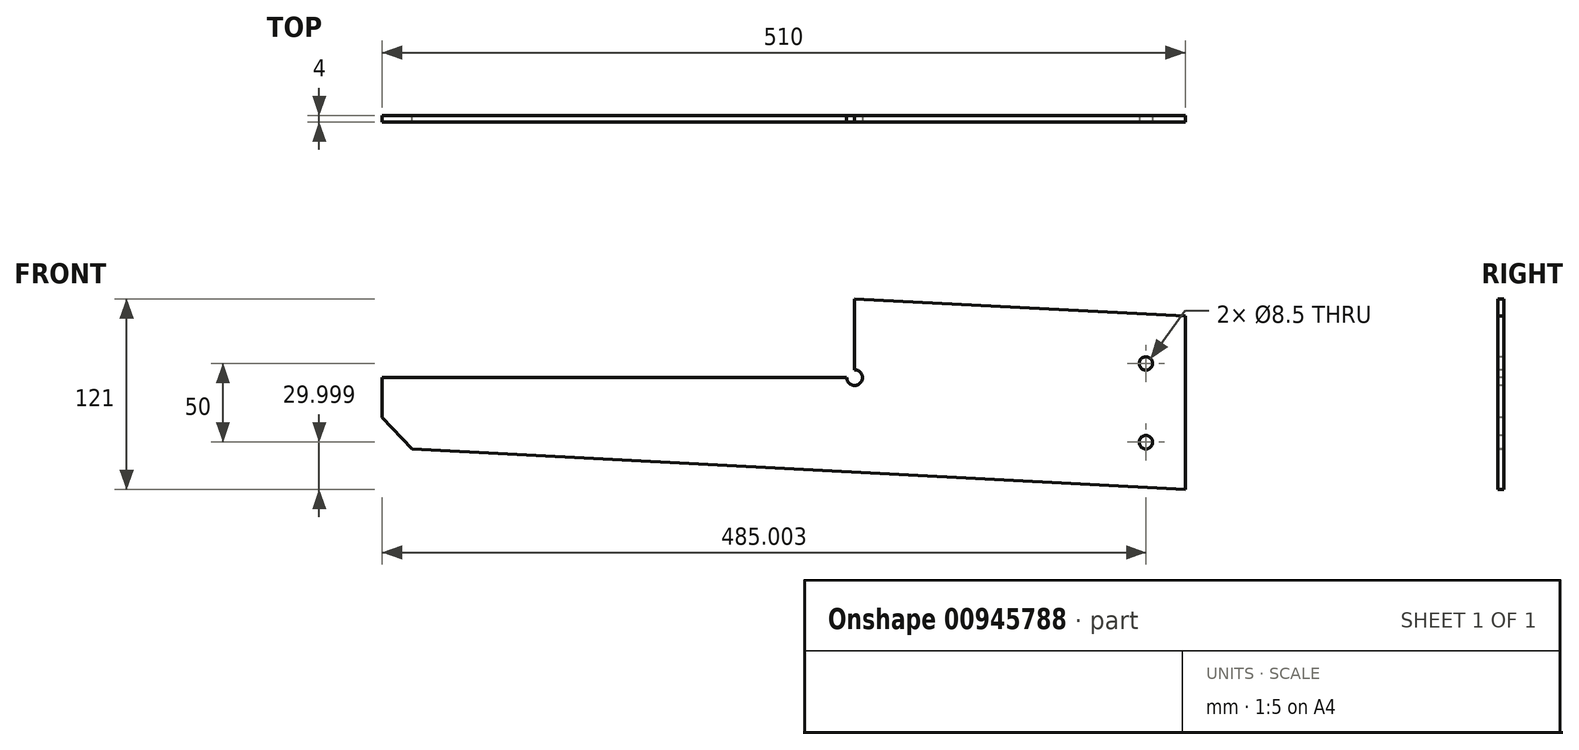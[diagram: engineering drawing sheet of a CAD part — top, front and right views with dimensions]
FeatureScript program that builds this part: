
annotation { "Feature Type Name" : "Feature", "Feature Type Description" : "" }
export const myFeature = defineFeature(function(context is Context, id is Id, definition is map)
    precondition{}
    {
        {
            var Q0;
            Q0=qCreatedBy(makeId("Front.planeOp"),FACE);
            var sketch = newSketch(context, id + "F0", { "sketchPlane" : qUnion([Q0])});
            skLineSegment(sketch, "E0", {"start": v(-207.34, -21.2) * mm, "end": v(92.66, -21.2) * mm});
            skLineSegment(sketch, "E1", {"start": v(92.66, -21.2) * mm, "end": v(92.66, 28.8) * mm});
            skLineSegment(sketch, "E2", {"start": v(92.66, 28.8) * mm, "end": v(302.66, 17.79) * mm});
            skLineSegment(sketch, "E3", {"start": v(302.66, 17.79) * mm, "end": v(302.66, -92.21) * mm});
            skLineSegment(sketch, "E4", {"start": v(302.66, -92.21) * mm, "end": v(-207.34, -65.48) * mm});
            skLineSegment(sketch, "E5", {"start": v(-207.34, -65.48) * mm, "end": v(-207.34, -21.2) * mm});
            skLineSegment(sketch, "E6", {"start": v(92.66, -21.2) * mm, "end": v(92.66, -81.2) * mm});
            skSolve(sketch);
        }
        {
            var Q0;
            Q0 = qSketchRegion(id + "F0", true);
            extrude(context, id + "F1", {"entities" : qUnion([Q0]), "depth" : 4 * mm, "offsetDistance" : 25 * mm});
        }
        {
            var Q0;
            Q0=makeQuery(id+"F1.opExtrude","SWEPT_EDGE",EDGE,{"disambiguationData":[OSD([sQuery(id+"F0.wireOp",EDGE,"E4"),sQuery(id+"F0.wireOp",EDGE,"E5")])]});
            chamfer(context, id + "F2", {"entities" : qUnion([Q0]), "width" : 20 * mm, "tangentPropagation" : true});
        }
        {
            var Q0;
            Q0=makeQuery(id+"F1.opExtrude","CAP_FACE",FACE,{"disambiguationData":[OSD([sQuery(id+"F0.wireOp",EDGE,"E0"),sQuery(id+"F0.wireOp",EDGE,"E1"),sQuery(id+"F0.wireOp",EDGE,"E2"),sQuery(id+"F0.wireOp",EDGE,"E3"),sQuery(id+"F0.wireOp",EDGE,"E4"),sQuery(id+"F0.wireOp",EDGE,"E5")])],"isStart":false});
            var sketch = newSketch(context, id + "F3", { "sketchPlane" : qUnion([Q0])});
            skCircle(sketch, "E7", {"center": v(92.66, -21.2) * mm, "radius": 5 * mm});
            skSolve(sketch);
        }
        {
            var Q0;
            Q0 = qSketchRegion(id + "F3", true);
            extrude(context, id + "F4", {"entities" : qUnion([Q0]), "operationType" : NewBodyOperationType.REMOVE, "oppositeDirection" : true, "depth" : 25 * mm, "offsetDistance" : 25 * mm});
        }
        {
            var Q0;
            Q0=makeQuery(id+"F1.opExtrude","CAP_FACE",FACE,{"disambiguationData":[OSD([sQuery(id+"F0.wireOp",EDGE,"E0"),sQuery(id+"F0.wireOp",EDGE,"E1"),sQuery(id+"F0.wireOp",EDGE,"E2"),sQuery(id+"F0.wireOp",EDGE,"E3"),sQuery(id+"F0.wireOp",EDGE,"E4"),sQuery(id+"F0.wireOp",EDGE,"E5")])],"isStart":false});
            var sketch = newSketch(context, id + "F5", { "sketchPlane" : qUnion([Q0])});
            skCircle(sketch, "E8", {"center": v(277.66, -12.21) * mm, "radius": 4.25 * mm});
            skCircle(sketch, "E9", {"center": v(277.66, -62.21) * mm, "radius": 4.25 * mm});
            skSolve(sketch);
        }
        {
            var Q0;
            Q0 = qSketchRegion(id + "F5", true);
            extrude(context, id + "F6", {"entities" : qUnion([Q0]), "operationType" : NewBodyOperationType.REMOVE, "oppositeDirection" : true, "depth" : 25 * mm, "offsetDistance" : 25 * mm});
        }
    });
